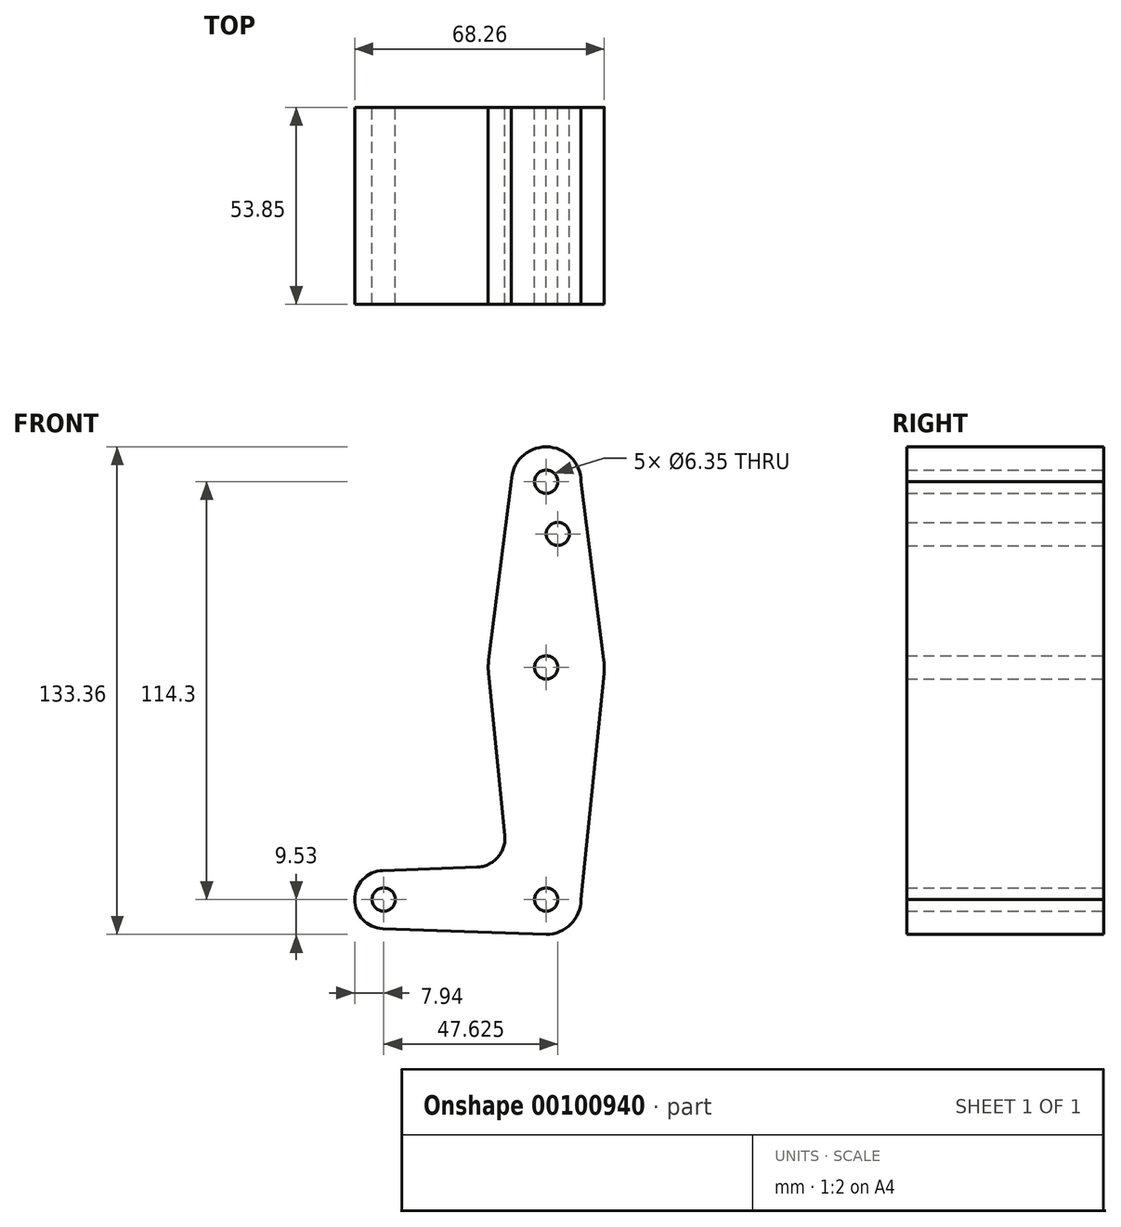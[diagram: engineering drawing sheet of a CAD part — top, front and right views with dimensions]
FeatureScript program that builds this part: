
annotation { "Feature Type Name" : "Feature", "Feature Type Description" : "" }
export const myFeature = defineFeature(function(context is Context, id is Id, definition is map)
    precondition{}
    {
        {
            var Q0;
            Q0=qCreatedBy(makeId("Front.planeOp"),FACE);
            var sketch = newSketch(context, id + "F0", { "sketchPlane" : qUnion([Q0])});
            skLineSegment(sketch, "E0", {"start": v(0, 0) * mm, "end": v(0, 114.3) * mm, "construction": true});
            skLineSegment(sketch, "E1", {"start": v(0, 0) * mm, "end": v(-44.45, 0) * mm, "construction": true});
            skCircle(sketch, "E2", {"center": v(0, 114.3) * mm, "radius": 9.53 * mm});
            skCircle(sketch, "E3", {"center": v(0, 63.5) * mm, "radius": 15.88 * mm});
            skCircle(sketch, "E4", {"center": v(0, 0) * mm, "radius": 9.53 * mm});
            skCircle(sketch, "E5", {"center": v(-44.45, 0) * mm, "radius": 7.94 * mm});
            skLineSegment(sketch, "E6", {"start": v(9.53, 114.3) * mm, "end": v(15.75, 65.5) * mm});
            skLineSegment(sketch, "E7", {"start": v(-9.52, 114.3) * mm, "end": v(-15.75, 65.5) * mm});
            skLineSegment(sketch, "E8", {"start": v(9.52, 0) * mm, "end": v(15.8, 61.9) * mm});
            skLineSegment(sketch, "E9", {"start": v(-11.34, 17.6) * mm, "end": v(-15.8, 61.91) * mm});
            skLineSegment(sketch, "E10", {"start": v(0, -9.53) * mm, "end": v(-44.73, -7.93) * mm});
            skLineSegment(sketch, "E11", {"start": v(-18.97, 8.85) * mm, "end": v(-44.73, 7.93) * mm});
            skCircle(sketch, "E12", {"center": v(0, 114.3) * mm, "radius": 3.18 * mm});
            skCircle(sketch, "E13", {"center": v(0, 63.5) * mm, "radius": 3.18 * mm});
            skCircle(sketch, "E14", {"center": v(0, 0) * mm, "radius": 3.18 * mm});
            skCircle(sketch, "E15", {"center": v(-44.45, 0) * mm, "radius": 3.18 * mm});
            skCircle(sketch, "E16", {"center": v(3.17, 100.03) * mm, "radius": 3.18 * mm});
            skPoint(sketch, "E17.newPointA", {"position": v(-9.57, 0) * mm});
            skArc(sketch, "E17.filletArc", {"start": v(-18.97, 8.85) * mm, "mid": v(-13.26, 11.57) * mm, "end": v(-11.34, 17.6) * mm});
            skSolve(sketch);
        }
        {
            var Q0;
            {var subQ1=sQuery(id+"F0.wireOp",EDGE,"E6");Q0=makeQuery(id+"F0.imprint","IMPRINT",FACE,{"disambiguationData":[TD([[makeQuery(id+"F0.imprint","IMPRINT",EDGE,{"derivedFrom":subQ1}),-1.0]])]});}
            var Q1;
            Q1=makeQuery(id+"F0.imprint","IMPRINT",FACE,{"disambiguationData":[TD([[makeQuery(id+"F0.imprint","IMPRINT",EDGE,{"derivedFrom":sQuery(id+"F0.wireOp",EDGE,"E12")}),-1.0]])]});
            var Q2;
            Q2=makeQuery(id+"F0.imprint","IMPRINT",FACE,{"disambiguationData":[TD([[makeQuery(id+"F0.imprint","IMPRINT",EDGE,{"derivedFrom":sQuery(id+"F0.wireOp",EDGE,"E13")}),-1.0]])]});
            var Q3;
            {var subQ0=sQuery(id+"F0.wireOp",EDGE,"E8");Q3=makeQuery(id+"F0.imprint","IMPRINT",FACE,{"disambiguationData":[TD([[makeQuery(id+"F0.imprint","IMPRINT",EDGE,{"derivedFrom":subQ0}),1.0]])]});}
            var Q4;
            Q4=makeQuery(id+"F0.imprint","IMPRINT",FACE,{"disambiguationData":[TD([[makeQuery(id+"F0.imprint","IMPRINT",EDGE,{"derivedFrom":sQuery(id+"F0.wireOp",EDGE,"E14")}),-1.0]])]});
            var Q5;
            Q5=makeQuery(id+"F0.imprint","IMPRINT",FACE,{"disambiguationData":[TD([[makeQuery(id+"F0.imprint","IMPRINT",EDGE,{"derivedFrom":sQuery(id+"F0.wireOp",EDGE,"E15")}),-1.0]])]});
            extrude(context, id + "F1", {"entities" : qUnion([Q0, Q1, Q2, Q3, Q4, Q5]), "depth" : 3.05 * mm});
        }
        {
            var Q0;
            Q0=makeQuery(id+"F1.opExtrude","CAP_FACE",FACE,{"disambiguationData":[OSD([sQuery(id+"F0.wireOp",EDGE,"E2"),sQuery(id+"F0.wireOp",EDGE,"E3"),sQuery(id+"F0.wireOp",EDGE,"E4"),sQuery(id+"F0.wireOp",EDGE,"E5"),sQuery(id+"F0.wireOp",EDGE,"E6"),sQuery(id+"F0.wireOp",EDGE,"E7"),sQuery(id+"F0.wireOp",EDGE,"E8"),sQuery(id+"F0.wireOp",EDGE,"E9"),sQuery(id+"F0.wireOp",EDGE,"E10"),sQuery(id+"F0.wireOp",EDGE,"E11"),sQuery(id+"F0.wireOp",EDGE,"E12"),sQuery(id+"F0.wireOp",EDGE,"E13"),sQuery(id+"F0.wireOp",EDGE,"E14"),sQuery(id+"F0.wireOp",EDGE,"E15"),sQuery(id+"F0.wireOp",EDGE,"E16"),sQuery(id+"F0.wireOp",EDGE,"E17.filletArc")])],"isStart":true});
            extrude(context, id + "F2", {"entities" : qUnion([Q0]), "operationType" : NewBodyOperationType.ADD, "depth" : 50.8 * mm});
        }
    });
